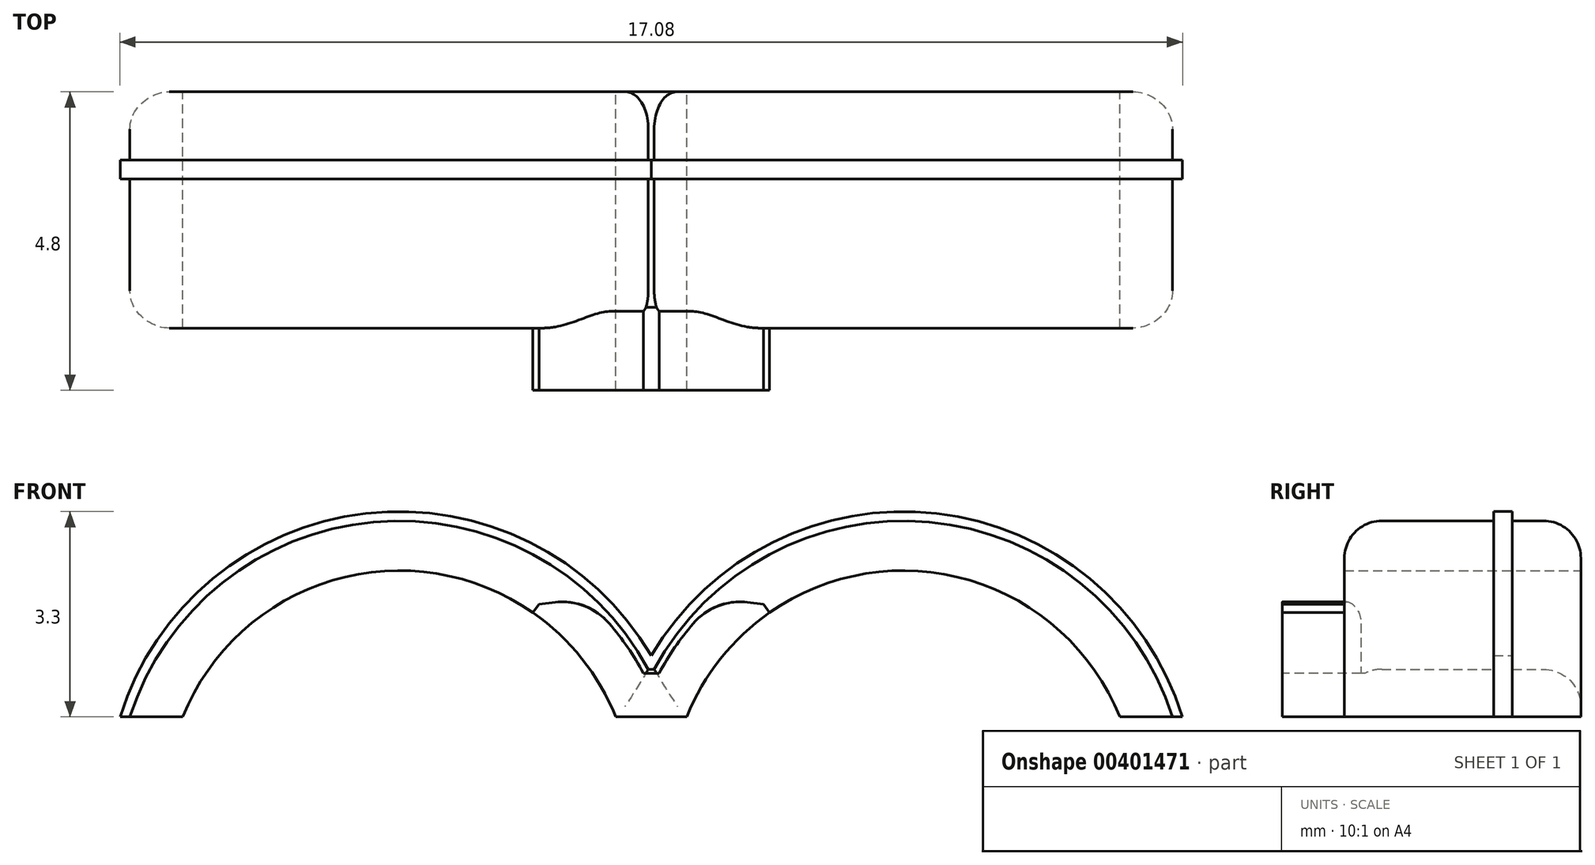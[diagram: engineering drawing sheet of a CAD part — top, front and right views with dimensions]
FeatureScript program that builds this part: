
annotation { "Feature Type Name" : "Feature", "Feature Type Description" : "" }
export const myFeature = defineFeature(function(context is Context, id is Id, definition is map)
    precondition{}
    {
        {
            var Q0;
            Q0=qCreatedBy(makeId("Front.planeOp"),FACE);
            var sketch = newSketch(context, id + "F0", { "sketchPlane" : qUnion([Q0])});
            skLineSegment(sketch, "E0", {"start": v(0, 0) * mm, "end": v(8.1, 0) * mm, "construction": true});
            skLineSegment(sketch, "E1", {"start": v(-4.33, 1.4) * mm, "end": v(-3.48, 1.4) * mm});
            skLineSegment(sketch, "E2.trimOffspring", {"start": v(3.48, 1.4) * mm, "end": v(4.62, 1.4) * mm});
            skLineSegment(sketch, "E3.trimOffspring", {"start": v(11.58, 1.4) * mm, "end": v(12.43, 1.4) * mm});
            skArc(sketch, "E4.trimOffspring", {"start": v(4, 2.16) * mm, "mid": v(-0.42, 4.53) * mm, "end": v(-4.33, 1.4) * mm});
            skArc(sketch, "E5.trimOffspring", {"start": v(3.48, 1.4) * mm, "mid": v(0, 3.75) * mm, "end": v(-3.48, 1.4) * mm});
            skArc(sketch, "E6.trimOffspring", {"start": v(12.43, 1.4) * mm, "mid": v(8.52, 4.53) * mm, "end": v(4.1, 2.16) * mm});
            skArc(sketch, "E7.trimOffspring", {"start": v(11.58, 1.4) * mm, "mid": v(8.1, 3.75) * mm, "end": v(4.62, 1.4) * mm});
            skLineSegment(sketch, "E8", {"start": v(4.05, 1.4) * mm, "end": v(4.05, 2.07) * mm, "construction": true});
            skLineSegment(sketch, "E9", {"start": v(4, 2.16) * mm, "end": v(4.1, 2.16) * mm});
            skSolve(sketch);
        }
        {
            var Q0;
            Q0=qSketchRegion(id+"F0",true);
            extrude(context, id + "F1", {"entities" : qUnion([Q0]), "depth" : 3.8 * mm, "offsetDistance" : 25 * mm});
        }
        {
            var Q0;
            Q0=makeQuery(id+"F1.opExtrude","CAP_EDGE",EDGE,{"disambiguationData":[OSD([sQuery(id+"F0.wireOp",EDGE,"E6.trimOffspring")])],"isStart":true});
            var Q1;
            Q1=makeQuery(id+"F1.opExtrude","CAP_EDGE",EDGE,{"disambiguationData":[OSD([sQuery(id+"F0.wireOp",EDGE,"E6.trimOffspring")])],"isStart":false});
            var Q2;
            Q2=makeQuery(id+"F1.opExtrude","CAP_EDGE",EDGE,{"disambiguationData":[OSD([sQuery(id+"F0.wireOp",EDGE,"E4.trimOffspring")])],"isStart":false});
            var Q3;
            Q3=makeQuery(id+"F1.opExtrude","CAP_EDGE",EDGE,{"disambiguationData":[OSD([sQuery(id+"F0.wireOp",EDGE,"E4.trimOffspring")])],"isStart":true});
            var Q4;
            Q4=makeQuery(id+"F1.opExtrude","CAP_EDGE",EDGE,{"disambiguationData":[OSD([sQuery(id+"F0.wireOp",EDGE,"E9")])],"isStart":false});
            var Q5;
            Q5=makeQuery(id+"F1.opExtrude","CAP_EDGE",EDGE,{"disambiguationData":[OSD([sQuery(id+"F0.wireOp",EDGE,"E9")])],"isStart":true});
            fillet(context, id + "F2", {"entities" : qUnion([Q0, Q1, Q2, Q3, Q4, Q5]), "radius" : 0.6 * mm, "allowEdgeOverflow" : false});
        }
        {
            var Q0;
            Q0=makeQuery(id+"F1.opExtrude","CAP_FACE",FACE,{"disambiguationData":[OSD([sQuery(id+"F0.wireOp",EDGE,"E1"),sQuery(id+"F0.wireOp",EDGE,"E2.trimOffspring"),sQuery(id+"F0.wireOp",EDGE,"E3.trimOffspring"),sQuery(id+"F0.wireOp",EDGE,"E4.trimOffspring"),sQuery(id+"F0.wireOp",EDGE,"E5.trimOffspring"),sQuery(id+"F0.wireOp",EDGE,"E6.trimOffspring"),sQuery(id+"F0.wireOp",EDGE,"E7.trimOffspring"),sQuery(id+"F0.wireOp",EDGE,"E9")])],"isStart":true});
            var Q1;
            Q1=makeQuery(id+"F1.opExtrude","CAP_FACE",FACE,{"disambiguationData":[OSD([sQuery(id+"F0.wireOp",EDGE,"E1"),sQuery(id+"F0.wireOp",EDGE,"E2.trimOffspring"),sQuery(id+"F0.wireOp",EDGE,"E3.trimOffspring"),sQuery(id+"F0.wireOp",EDGE,"E4.trimOffspring"),sQuery(id+"F0.wireOp",EDGE,"E5.trimOffspring"),sQuery(id+"F0.wireOp",EDGE,"E6.trimOffspring"),sQuery(id+"F0.wireOp",EDGE,"E7.trimOffspring"),sQuery(id+"F0.wireOp",EDGE,"E9")])],"isStart":false});
            cPlane(context, id + "F3", {"entities" : qUnion([Q0, Q1]), "cplaneType" : CPlaneType.MID_PLANE, "offset" : 25 * mm, "width" : 150 * mm, "height" : 150 * mm});
        }
        {
            var Q0;
            Q0=qCreatedBy(id+"F3.planeOp",FACE);
            cPlane(context, id + "F4", {"entities" : qUnion([Q0]), "cplaneType" : CPlaneType.OFFSET, "offset" : 0.8 * mm, "width" : 150 * mm, "height" : 150 * mm});
        }
        {
            var Q0;
            Q0=qCreatedBy(id+"F4.planeOp",FACE);
            var sketch = newSketch(context, id + "F5", { "sketchPlane" : qUnion([Q0])});
            skArc(sketch, "E10.0", {"start": v(-12.43, 1.4) * mm, "mid": v(-8.52, 4.53) * mm, "end": v(-4.1, 2.16) * mm});
            skArc(sketch, "E10.1", {"start": v(-4, 2.16) * mm, "mid": v(0.42, 4.53) * mm, "end": v(4.33, 1.4) * mm});
            skLineSegment(sketch, "E10.2", {"start": v(-4.1, 2.16) * mm, "end": v(-4, 2.16) * mm});
            skArc(sketch, "E11.0", {"start": v(-4.05, 2.38) * mm, "mid": v(0.54, 4.67) * mm, "end": v(4.49, 1.4) * mm});
            skArc(sketch, "E11.1", {"start": v(-12.59, 1.4) * mm, "mid": v(-8.64, 4.67) * mm, "end": v(-4.05, 2.38) * mm});
            skLineSegment(sketch, "E12", {"start": v(-12.59, 1.4) * mm, "end": v(-12.43, 1.4) * mm});
            skLineSegment(sketch, "E13", {"start": v(4.33, 1.4) * mm, "end": v(4.49, 1.4) * mm});
            skSolve(sketch);
        }
        {
            var Q0;
            Q0 = qSketchRegion(id + "F5", true);
            extrude(context, id + "F6", {"entities" : qUnion([Q0]), "operationType" : NewBodyOperationType.ADD, "oppositeDirection" : true, "depth" : 0.3 * mm, "offsetDistance" : 25 * mm});
        }
        {
            var Q0;
            Q0=makeQuery(id+"F1.opExtrude","CAP_FACE",FACE,{"disambiguationData":[OSD([sQuery(id+"F0.wireOp",EDGE,"E1"),sQuery(id+"F0.wireOp",EDGE,"E2.trimOffspring"),sQuery(id+"F0.wireOp",EDGE,"E3.trimOffspring"),sQuery(id+"F0.wireOp",EDGE,"E4.trimOffspring"),sQuery(id+"F0.wireOp",EDGE,"E5.trimOffspring"),sQuery(id+"F0.wireOp",EDGE,"E6.trimOffspring"),sQuery(id+"F0.wireOp",EDGE,"E7.trimOffspring"),sQuery(id+"F0.wireOp",EDGE,"E9")])],"isStart":true});
            cPlane(context, id + "F7", {"entities" : qUnion([Q0]), "cplaneType" : CPlaneType.OFFSET, "offset" : 4.8 * mm, "oppositeDirection" : true, "width" : 150 * mm, "height" : 150 * mm});
        }
        {
            var Q0;
            Q0=qCreatedBy(id+"F7.planeOp",FACE);
            var sketch = newSketch(context, id + "F8", { "sketchPlane" : qUnion([Q0])});
            skLineSegment(sketch, "E14.0", {"start": v(-3.48, 1.4) * mm, "end": v(-4.62, 1.4) * mm});
            skArc(sketch, "E14.1", {"start": v(-5.95, 3.07) * mm, "mid": v(-5.16, 2.33) * mm, "end": v(-4.62, 1.4) * mm});
            skArc(sketch, "E14.2", {"start": v(-3.48, 1.4) * mm, "mid": v(-2.94, 2.33) * mm, "end": v(-2.15, 3.07) * mm});
            skArc(sketch, "E15.0", {"start": v(-3.92, 2.1) * mm, "mid": v(-3.33, 2.95) * mm, "end": v(-2.55, 3.65) * mm});
            skArc(sketch, "E15.1", {"start": v(-5.55, 3.65) * mm, "mid": v(-4.77, 2.95) * mm, "end": v(-4.18, 2.1) * mm});
            skLineSegment(sketch, "E16", {"start": v(-2.15, 3.07) * mm, "end": v(-2.55, 3.65) * mm});
            skLineSegment(sketch, "E17", {"start": v(-3.92, 2.1) * mm, "end": v(-4.18, 2.1) * mm});
            skPoint(sketch, "E18.orphan", {"position": v(3.48, 1.4) * mm});
            skLineSegment(sketch, "E19", {"start": v(-5.55, 3.65) * mm, "end": v(-5.95, 3.07) * mm});
            skPoint(sketch, "E20.orphan", {"position": v(-11.58, 1.4) * mm});
            skSolve(sketch);
        }
        {
            var Q0;
            Q0 = qSketchRegion(id + "F8", true);
            extrude(context, id + "F9", {"entities" : qUnion([Q0]), "operationType" : NewBodyOperationType.ADD, "endBound" : BoundingType.UP_TO_NEXT, "depth" : 25 * mm, "offsetDistance" : 25 * mm});
        }
        {
            var Q0;
            Q0=makeQuery(id+"F9.opExtrude","SWEPT_EDGE",EDGE,{"disambiguationData":[OSD([sQuery(id+"F8.wireOp",EDGE,"E15.0"),sQuery(id+"F8.wireOp",EDGE,"E16")])]});
            var Q1;
            Q1=makeQuery(id+"F9.opExtrude","SWEPT_EDGE",EDGE,{"disambiguationData":[OSD([sQuery(id+"F8.wireOp",EDGE,"E15.1"),sQuery(id+"F8.wireOp",EDGE,"E19")])]});
            chamfer(context, id + "F10", {"entities" : qUnion([Q0, Q1]), "width" : 0.5 * mm, "tangentPropagation" : true});
        }
        {
            var Q0;
            {var subQ0=sQuery(id+"F8.wireOp",EDGE,"E15.1");Q0=makeQuery(id+"F10.opChamfer","BLEND_EDGE",EDGE,{"blendedFrom":[makeQuery(id+"F9.opExtrude","SWEPT_EDGE",EDGE,{"disambiguationData":[OSD([subQ0,sQuery(id+"F8.wireOp",EDGE,"E19")])]}),makeQuery(id+"F9.opExtrude","SWEPT_FACE",FACE,{"disambiguationData":[OSD([subQ0])]})],"blendedInto":[makeQuery(id+"F9.opExtrude","SWEPT_FACE",FACE,{"disambiguationData":[OSD([subQ0])]})]});}
            var Q1;
            {var subQ0=sQuery(id+"F8.wireOp",EDGE,"E15.0");Q1=makeQuery(id+"F10.opChamfer","BLEND_EDGE",EDGE,{"blendedFrom":[makeQuery(id+"F9.opExtrude","SWEPT_EDGE",EDGE,{"disambiguationData":[OSD([subQ0,sQuery(id+"F8.wireOp",EDGE,"E16")])]}),makeQuery(id+"F9.opExtrude","SWEPT_FACE",FACE,{"disambiguationData":[OSD([subQ0])]})],"blendedInto":[makeQuery(id+"F9.opExtrude","SWEPT_FACE",FACE,{"disambiguationData":[OSD([subQ0])]})]});}
            fillet(context, id + "F11", {"entities" : qUnion([Q0, Q1]), "radius" : 1 * mm, "tangentPropagation" : true, "allowEdgeOverflow" : false});
        }
    });
